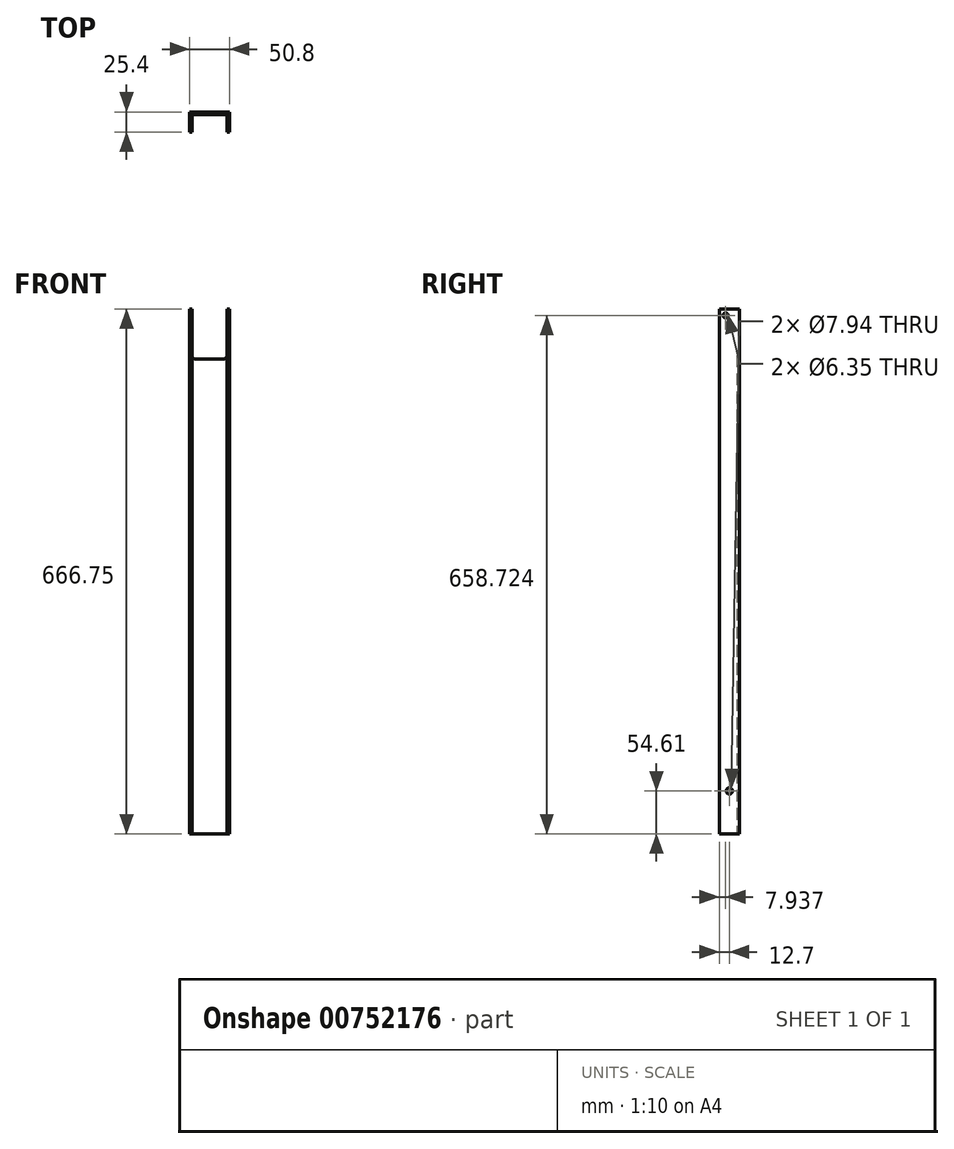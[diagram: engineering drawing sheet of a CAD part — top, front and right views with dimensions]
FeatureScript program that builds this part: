
annotation { "Feature Type Name" : "Feature", "Feature Type Description" : "" }
export const myFeature = defineFeature(function(context is Context, id is Id, definition is map)
    precondition{}
    {
        {
            var Q0;
            Q0=qCreatedBy(makeId("Top.planeOp"),FACE);
            var sketch = newSketch(context, id + "F0", { "sketchPlane" : qUnion([Q0])});
            skLineSegment(sketch, "E0", {"start": v(-25.4, -12.7) * mm, "end": v(-22.22, -12.7) * mm});
            skLineSegment(sketch, "E1", {"start": v(-22.22, -12.7) * mm, "end": v(-22.23, 9.53) * mm});
            skLineSegment(sketch, "E2", {"start": v(-22.23, 9.53) * mm, "end": v(22.22, 9.53) * mm});
            skLineSegment(sketch, "E3", {"start": v(22.23, 9.53) * mm, "end": v(22.23, -12.7) * mm});
            skLineSegment(sketch, "E4", {"start": v(22.22, -12.7) * mm, "end": v(25.4, -12.7) * mm});
            skLineSegment(sketch, "E5", {"start": v(25.4, -12.7) * mm, "end": v(25.4, 12.7) * mm});
            skLineSegment(sketch, "E6", {"start": v(25.4, 12.7) * mm, "end": v(-25.4, 12.7) * mm});
            skLineSegment(sketch, "E7", {"start": v(-25.4, 12.7) * mm, "end": v(-25.4, -12.7) * mm});
            skLineSegment(sketch, "E8.bottom", {"start": v(25.65, 16.68) * mm, "end": v(101.85, 16.68) * mm, "construction": true});
            skLineSegment(sketch, "E8.top", {"start": v(25.65, -16.68) * mm, "end": v(101.85, -16.68) * mm, "construction": true});
            skLineSegment(sketch, "E8.left", {"start": v(25.65, 16.68) * mm, "end": v(25.65, -16.68) * mm, "construction": true});
            skLineSegment(sketch, "E8.right", {"start": v(101.85, 16.68) * mm, "end": v(101.85, -16.68) * mm, "construction": true});
            skCircle(sketch, "E9", {"center": v(44.7, 0) * mm, "radius": 4.17 * mm, "construction": true});
            skCircle(sketch, "E10", {"center": v(82.8, 0) * mm, "radius": 4.17 * mm, "construction": true});
            skCircle(sketch, "E11.MirrorC", {"center": v(-44.7, 0) * mm, "radius": 4.17 * mm, "construction": true});
            skLineSegment(sketch, "E12.MirrorCS", {"start": v(-101.85, 16.68) * mm, "end": v(-101.85, -16.68) * mm, "construction": true});
            skLineSegment(sketch, "E13.MirrorCS", {"start": v(-25.65, 16.68) * mm, "end": v(-25.65, -16.68) * mm, "construction": true});
            skLineSegment(sketch, "E14.MirrorCS", {"start": v(-25.65, -16.68) * mm, "end": v(-101.85, -16.68) * mm, "construction": true});
            skCircle(sketch, "E15.MirrorC", {"center": v(-82.8, 0) * mm, "radius": 4.17 * mm, "construction": true});
            skLineSegment(sketch, "E16.MirrorCS", {"start": v(-25.65, 16.68) * mm, "end": v(-101.85, 16.68) * mm, "construction": true});
            skLineSegment(sketch, "E17", {"start": v(-12.7, -19.05) * mm, "end": v(-12.7, 6.35) * mm, "construction": true});
            skLineSegment(sketch, "E18", {"start": v(-12.7, 6.35) * mm, "end": v(12.7, 6.35) * mm, "construction": true});
            skLineSegment(sketch, "E19", {"start": v(12.7, 6.35) * mm, "end": v(12.7, -19.05) * mm, "construction": true});
            skLineSegment(sketch, "E20", {"start": v(12.7, -19.05) * mm, "end": v(9.53, -19.05) * mm, "construction": true});
            skLineSegment(sketch, "E21", {"start": v(9.53, -19.05) * mm, "end": v(9.53, 3.18) * mm, "construction": true});
            skLineSegment(sketch, "E22", {"start": v(9.53, 3.18) * mm, "end": v(-9.53, 3.17) * mm, "construction": true});
            skLineSegment(sketch, "E23", {"start": v(-9.53, 3.17) * mm, "end": v(-9.52, -19.05) * mm, "construction": true});
            skLineSegment(sketch, "E24", {"start": v(-9.52, -19.05) * mm, "end": v(-12.7, -19.05) * mm, "construction": true});
            skLineSegment(sketch, "E25.bottom", {"start": v(22.23, 7.14) * mm, "end": v(17.22, 7.14) * mm, "construction": true});
            skLineSegment(sketch, "E25.top", {"start": v(22.23, -7.14) * mm, "end": v(17.22, -7.14) * mm, "construction": true});
            skLineSegment(sketch, "E25.left", {"start": v(22.23, 7.14) * mm, "end": v(22.23, -7.14) * mm, "construction": true});
            skLineSegment(sketch, "E25.right", {"start": v(17.22, 7.14) * mm, "end": v(17.22, -7.14) * mm, "construction": true});
            skLineSegment(sketch, "E26.bottom", {"start": v(-22.23, -7.14) * mm, "end": v(-17.22, -7.14) * mm, "construction": true});
            skLineSegment(sketch, "E26.top", {"start": v(-22.23, 7.14) * mm, "end": v(-17.22, 7.14) * mm, "construction": true});
            skLineSegment(sketch, "E26.left", {"start": v(-22.23, -7.14) * mm, "end": v(-22.23, 7.14) * mm, "construction": true});
            skLineSegment(sketch, "E26.right", {"start": v(-17.22, -7.14) * mm, "end": v(-17.22, 7.14) * mm, "construction": true});
            skSolve(sketch);
        }
        {
            var Q0;
            Q0=makeQuery(id+"F0.imprint","IMPRINT",FACE,{"disambiguationData":[TD([[makeQuery(id+"F0.imprint","IMPRINT",EDGE,{"derivedFrom":sQuery(id+"F0.wireOp",EDGE,"E0")}),1.0]])]});
            extrude(context, id + "F1", {"entities" : qUnion([Q0]), "depth" : 666.75 * mm, "offsetDistance" : 25.4 * mm});
        }
        {
            var Q0;
            Q0=makeQuery(id+"F1.opExtrude","SWEPT_FACE",FACE,{"disambiguationData":[OSD([sQuery(id+"F0.wireOp",EDGE,"E5")])]});
            var sketch = newSketch(context, id + "F2", { "sketchPlane" : qUnion([Q0])});
            skLineSegment(sketch, "E27.bottom", {"start": v(-16.68, -2.54) * mm, "end": v(16.68, -2.54) * mm, "construction": true});
            skLineSegment(sketch, "E27.top", {"start": v(-16.68, 73.66) * mm, "end": v(16.68, 73.66) * mm, "construction": true});
            skLineSegment(sketch, "E27.left", {"start": v(-16.68, -2.54) * mm, "end": v(-16.68, 73.66) * mm, "construction": true});
            skLineSegment(sketch, "E27.right", {"start": v(16.68, -2.54) * mm, "end": v(16.68, 73.66) * mm, "construction": true});
            skCircle(sketch, "E28", {"center": v(0, 16.5) * mm, "radius": 3.97 * mm});
            skCircle(sketch, "E29", {"center": v(0, 54.6) * mm, "radius": 3.97 * mm});
            skSolve(sketch);
        }
        {
            var Q0;
            Q0 = qSketchRegion(id + "F2", true);
            var Q1;
            Q1=makeQuery(id+"F1.opExtrude","SWEPT_FACE",FACE,{"disambiguationData":[OSD([sQuery(id+"F0.wireOp",EDGE,"E7")])]});
            extrude(context, id + "F3", {"entities" : qUnion([Q0]), "operationType" : NewBodyOperationType.REMOVE, "endBound" : BoundingType.UP_TO_SURFACE, "oppositeDirection" : true, "depth" : 25.4 * mm, "endBoundEntityFace" : qUnion([Q1]), "offsetDistance" : 25.4 * mm});
        }
        {
            var Q0;
            Q0=makeQuery(id+"F1.opExtrude","SWEPT_FACE",FACE,{"disambiguationData":[OSD([sQuery(id+"F0.wireOp",EDGE,"E5")])]});
            var sketch = newSketch(context, id + "F4", { "sketchPlane" : qUnion([Q0])});
            skCircle(sketch, "E30", {"center": v(-4.76, 658.72) * mm, "radius": 3.18 * mm});
            skSolve(sketch);
        }
        {
            var Q0;
            Q0 = qSketchRegion(id + "F4", true);
            var Q1;
            Q1=makeQuery(id+"F1.opExtrude","SWEPT_FACE",FACE,{"disambiguationData":[OSD([sQuery(id+"F0.wireOp",EDGE,"E7")])]});
            extrude(context, id + "F5", {"entities" : qUnion([Q0]), "operationType" : NewBodyOperationType.REMOVE, "endBound" : BoundingType.UP_TO_SURFACE, "oppositeDirection" : true, "depth" : 25.4 * mm, "endBoundEntityFace" : qUnion([Q1]), "offsetDistance" : 25.4 * mm});
        }
        {
            var Q0;
            Q0=makeQuery(id+"F1.opExtrude","SWEPT_FACE",FACE,{"disambiguationData":[OSD([sQuery(id+"F0.wireOp",EDGE,"E6")])]});
            var sketch = newSketch(context, id + "F6", { "sketchPlane" : qUnion([Q0])});
            skLineSegment(sketch, "E31", {"start": v(0, 672.54) * mm, "end": v(0, 626.5) * mm, "construction": true});
            skPoint(sketch, "E31.startSnap0", {"position": v(0, 666.75) * mm});
            skLineSegment(sketch, "E32.bottom", {"start": v(-22.23, 666.75) * mm, "end": v(22.23, 666.75) * mm});
            skLineSegment(sketch, "E32.top", {"start": v(-17.46, 603.25) * mm, "end": v(17.46, 603.25) * mm});
            skLineSegment(sketch, "E32.left", {"start": v(-22.23, 666.75) * mm, "end": v(-22.22, 608.01) * mm});
            skLineSegment(sketch, "E32.right", {"start": v(22.23, 666.75) * mm, "end": v(22.23, 608.01) * mm});
            skArc(sketch, "E33", {"start": v(-22.22, 608.01) * mm, "mid": v(-20.83, 604.64) * mm, "end": v(-17.46, 603.25) * mm});
            skArc(sketch, "E34", {"start": v(17.46, 603.25) * mm, "mid": v(20.83, 604.64) * mm, "end": v(22.23, 608.01) * mm});
            skPoint(sketch, "E35.orphan", {"position": v(-22.22, 603.25) * mm});
            skPoint(sketch, "E36.orphan", {"position": v(22.23, 603.25) * mm});
            skSolve(sketch);
        }
        {
            var Q0;
            Q0 = qSketchRegion(id + "F6", true);
            extrude(context, id + "F7", {"entities" : qUnion([Q0]), "operationType" : NewBodyOperationType.REMOVE, "oppositeDirection" : true, "depth" : 25.4 * mm, "offsetDistance" : 25.4 * mm});
        }
        {
            var Q0;
            Q0 = qSketchRegion(id + "F0", true);
            extrude(context, id + "F8", {"entities" : qUnion([Q0]), "operationType" : NewBodyOperationType.ADD, "depth" : 25.4 * mm, "offsetDistance" : 25.4 * mm});
        }
    });
